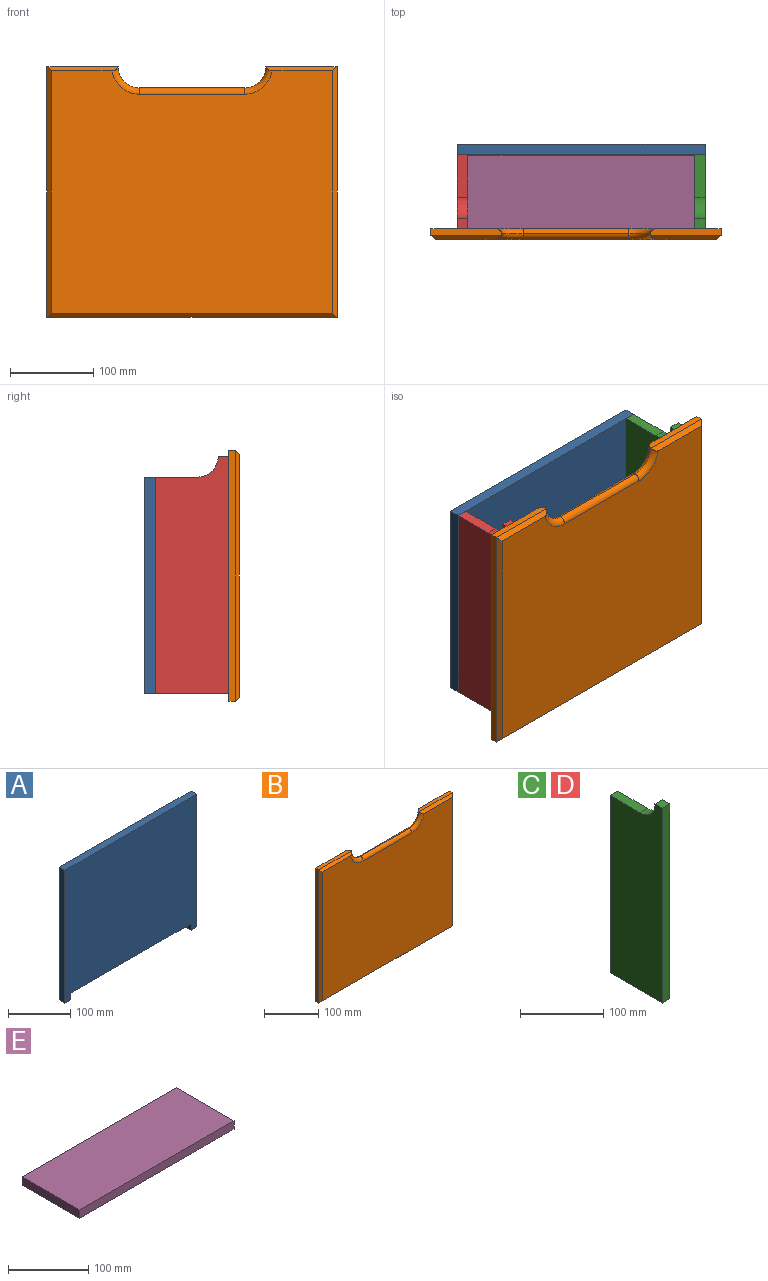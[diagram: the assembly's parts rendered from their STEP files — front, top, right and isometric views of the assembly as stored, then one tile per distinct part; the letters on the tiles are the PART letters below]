
ASSEMBLY  parts=5 mates=4
PART A: 10 faces, bbox 298.5x12.7x260.4 mm
  f0: plane 12.7x12.7mm, normal (1,0,0), area 161.3mm2, adj f1,f7,f8,f9
  f1: plane 273.05x12.7mm, normal (0,0,-1), area 3467.7mm2, adj f0,f2,f8,f9
  f2: plane 12.7x12.7mm, normal (-1,0,0), area 161.3mm2, adj f1,f3,f8,f9
  f3: plane 12.7x12.7mm, normal (0,0,-1), area 161.3mm2, adj f2,f4,f8,f9
  f4: plane 260.35x12.7mm, normal (1,0,0), area 3306.4mm2, adj f3,f5,f8,f9
  f5: plane 298.45x12.7mm, normal (0,0,1), area 3790.3mm2, adj f4,f6,f8,f9
  f6: plane 260.35x12.7mm, normal (-1,0,0), area 3306.4mm2, adj f5,f7,f8,f9
  f7: plane 12.7x12.7mm, normal (0,0,-1), area 161.3mm2, adj f0,f6,f8,f9
  f8: plane 298.45x260.35mm, normal (0,-1,0), area 74233.7mm2, adj f0,f1,f2,f3,f4,f5,f6,f7
  f9: plane 298.45x260.35mm, normal (0,1,0), area 74233.7mm2, adj f0,f1,f2,f3,f4,f5,f6,f7
PART B: 18 faces, bbox 349.3x12.7x301.6 mm
  f0: plane 85.62x7.62mm, normal (0,0,1), area 640.5mm2, adj f4,f6,f11,f12,f13
  f1: plane 85.62x7.62mm, normal (0,0,1), area 640.5mm2, adj f2,f6,f7,f16,f17
  f2: plane 301.63x7.62mm, normal (-1,0,0), area 2298.4mm2, adj f1,f3,f6,f8
  f3: plane 349.25x7.62mm, normal (0,0,-1), area 2661.3mm2, adj f2,f4,f6,f9
  f4: plane 301.63x7.62mm, normal (1,0,0), area 2298.4mm2, adj f0,f3,f6,f10
  f5: plane 339.09x291.47mm, normal (0,-1,0), area 93906mm2, adj f7,f8,f9,f10,f11,f12,f14,f16
  f6: plane 349.25x301.63mm, normal (0,1,0), area 99436.3mm2, adj f0,f1,f2,f3,f4,f13,f15,f17
  f7: plane 85.29x5.08mm, normal (0,-0.71,0.71), area 581.6mm2, adj f1,f5,f8,f16
  f8: plane 301.63x5.08mm, normal (-0.71,-0.71,0), area 2130.4mm2, adj f2,f5,f7,f9
  f9: plane 349.25x5.08mm, normal (0,-0.71,-0.71), area 2472.6mm2, adj f3,f5,f8,f10
  f10: plane 301.63x5.08mm, normal (0.71,-0.71,0), area 2130.4mm2, adj f4,f5,f9,f11
  f11: plane 85.29x5.08mm, normal (0,-0.71,0.71), area 581.6mm2, adj f0,f5,f10,f12
  f12: torus R=33.02mm, axis (0,-1,0), area 447.6mm2, adj f0,f5,f11,f13,f14
  f13: torus R=33.02mm, axis (0,-1,0), area 478.6mm2, adj f0,f6,f12,f15
  f14: cylinder r=7.62mm len=127mm, axis (1,0,0), area 1358.1mm2, adj f5,f12,f15,f16
  f15: cylinder r=7.62mm len=127mm, axis (-1,0,0), area 1358.1mm2, adj f6,f13,f14,f17
  f16: torus R=33.02mm, axis (0,-1,0), area 447.6mm2, adj f1,f5,f7,f14,f17
  f17: torus R=33.02mm, axis (0,-1,0), area 478.6mm2, adj f1,f6,f15,f16
PART C: 8 faces, bbox 12.7x88.9x285.8 mm
  f0: plane 260.35x12.7mm, normal (0,1,0), area 3306.4mm2, adj f1,f5,f6,f7
  f1: plane 50.8x12.7mm, normal (0,0,1), area 645.2mm2, adj f0,f2,f6,f7
  f2: cylinder r=25.4mm len=25.4mm, axis (-1,0,0), area 506.7mm2, adj f1,f3,f6,f7
  f3: plane 12.7x12.7mm, normal (0,0,1), area 161.3mm2, adj f2,f4,f6,f7
  f4: plane 285.75x12.7mm, normal (0,-1,0), area 3629mm2, adj f3,f5,f6,f7
  f5: plane 88.9x12.7mm, normal (0,0,-1), area 1129mm2, adj f0,f4,f6,f7
  f6: plane 285.75x88.9mm, normal (1,0,0), area 23606.1mm2, adj f0,f1,f2,f3,f4,f5
  f7: plane 285.75x88.9mm, normal (-1,0,0), area 23606.1mm2, adj f0,f1,f2,f3,f4,f5
PART D: same geometry as C
PART E: 6 faces, bbox 273.1x101.6x12.7 mm
  f0: plane 273.05x12.7mm, normal (0,1,0), area 3467.7mm2, adj f1,f3,f4,f5
  f1: plane 101.6x12.7mm, normal (-1,0,0), area 1290.3mm2, adj f0,f2,f4,f5
  f2: plane 273.05x12.7mm, normal (0,-1,0), area 3467.7mm2, adj f1,f3,f4,f5
  f3: plane 101.6x12.7mm, normal (1,0,0), area 1290.3mm2, adj f0,f2,f4,f5
  f4: plane 273.05x101.6mm, normal (0,0,1), area 27741.9mm2, adj f0,f1,f2,f3
  f5: plane 273.05x101.6mm, normal (0,0,-1), area 27741.9mm2, adj f0,f1,f2,f3
PLACE A t=(-68.14,85.8,-340.08)mm
PLACE B t=(-26.32,-28.5,-1.2)mm
PLACE C t=(108.33,170.79,143.79)mm
PLACE D t=(-177.42,170.79,143.79)mm
PLACE E t=(-97.38,-166.4,-157.27)mm
MATE fastened C.f7 <-> E.f3  axis (-1,0,0) through (108.33,-28.5,-157.27)mm
MATE fastened D.f6 <-> E.f1  axis (1,0,0) through (-164.72,-28.5,-157.27)mm
MATE fastened E.f2 <-> B.f6  axis (0,-1,0) through (-28.2,-28.5,-157.27)mm
MATE fastened A.f2 <-> E.f3  axis (-1,0,0) through (108.33,73.1,-157.27)mm
